# Revit family: Shower-Handshower_Kit-KOHLER-COMPOSED-K-73085T
name_source: partatom
category: Plumbing Fixtures
revit_build: Autodesk Revit 2017 (Build: 20160225_1515(x64)
units: mm (PartAtom-declared; Revit-internal decimal feet)

## family parameters
Cut with Voids When Loaded = No
Host = Face
OmniClass Number = 23.31.17.00
OmniClass Title = Showers
Part Type = Normal
Room Calculation Point = No
Round Connector Dimension = Use Diameter
Shared = No

## types (2) — shared parameters
ADA Compliant = No
Assembly Code = D2010700
CW Connection = Yes
Cold Water Inlet = Cold Water Inlet
Date Modified = 24/09/2020
Default Elevation = 36"
Description = Cylinder Side Water Divider and Hand Shower
Drain Included = No
Flow Rate = 3 GPM
HW Connection = Yes
Height = 10 7/16"
Height Of Handle = 2 5/8"
Hot Water Inlet = Hot Water Inlet
Length = 2 1/2"
Manufacturer = KOHLER Co.
Master Format 2014 = 22 42 23
Master Format 2014 Name = Residential Showers
Material = Premium Metal Construction
Panel Thickness = 0"
Pressure = 70.00 psi
Product Documentation Link = https://files.kohler.com.cn
Product Name = COMPOSED
Product Page URL = https://www.kohler.com.cn
URL = https://www.kohler.com.cn
Vent Connection = No
Waste Connection = No
Waste Water Outlet = Waste Water Outlet
WaterSense Certified = No

## per-type parameters (varying)
| type | Finish | Handle Material | Model | Type |
| B9ACH,BV-Roman Copper | Kohler-Metal-BV-Roman_Copper | Kohler-Glass-ACH-Amber_Gold_Glaze | K-73085T-B9ACH-BV | 1 |
| B9GCH,TT-Titanium Silver | Kohler-Metal-TT-Titanium_Silver | Kohler-Glass-GCH-Ink_Ash_Glass | K-73085T-B9GCH-TT | 2 |

## geometry (parser evidence)
native form markers: Sweep x8
no freeform markers — native parametric forms only
